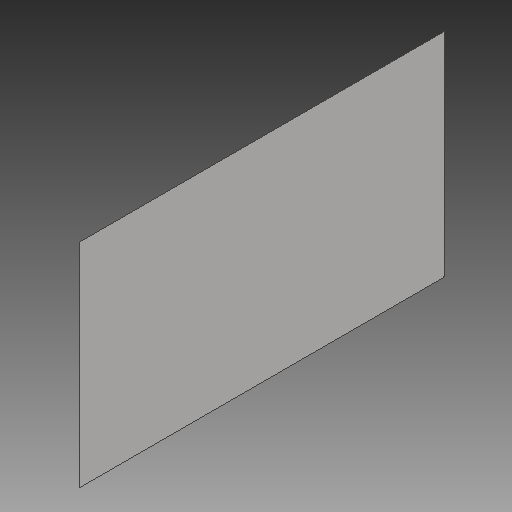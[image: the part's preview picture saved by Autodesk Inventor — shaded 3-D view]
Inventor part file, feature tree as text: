
AUTODESK INVENTOR PART (.ipt)
format: ipt  version: 2018.2 (Build 222227000, 227)  size: 76,288 bytes
history: native  units: mm
features: other x3, sketch x1
ambient origin geometry x8: Origin, YZ Plane, XZ Plane, XY Plane, X Axis, Y Axis, Z Axis, Center Point
bodies: Volumenkörper1 (feature_tree)
feature tree (4):
  other  "Wand2.ipt"
  other  "Volumenkörper1::Wand2.ipt"
  other  "Bezeichnung1"
  sketch  "Skizze1"  dims[d0=10.0mm]
